# Revit family: Haworth_Tibas_Desk_MeetingTable_AP_PRELIMINARY1
name_source: partatom
category: Furniture
units: mm (PartAtom-declared; Revit-internal decimal feet)

## family parameters
Always vertical = Yes
Cut with Voids When Loaded = No
OmniClass Number = 23.40.70.14.64.11
OmniClass Title = Office Furniture
Room Calculation Point = No
Shared = No
Work Plane-Based = No

## types (2) — shared parameters
Actual Depth = 1400 mm  [stored 4.59318 ft]
Actual Height = 835 mm
Actual Width = 1400 mm  [stored 4.59318 ft]
Assembly Code = E2020200
Cable Tray Finish = Haworth _ Paint _ Metallic Silver
Cable Tray Width = 1000 mm  [stored 3.28084 ft]
Description = Haworth - Tibas - Desk - Meeting Table
Flip Top Width = 200 mm  [stored 0.656168 ft]
Leg Height = 800 mm  [stored 2.62467 ft]
Manufacturer = Haworth
Model = SYTBMNXXXX
Product URL = https://www.haworth.com
Revision Number = 1
Size = Verify Final Dim.w/ Haworth
Trim Finish = Haworth _ Polymer _ Undecided
URL = https://www.haworth.com
Warranty = http://www.haworth.com

## per-type parameters (varying)
| type | Beam Width | Cable Tray | Flip Top Cable Outlet | Flush Table | Leg Depth | Leg Width | Non Flush Table |
| 1400w x 1400d - Non Flush | 1200 mm | No | No | No | 1200 mm | 150 mm | Yes |
| 1400w x 1400d - Flush | 1400 mm  [stored 4.59318 ft] | Yes | Yes | Yes | 1400 mm  [stored 4.59318 ft] | 50 mm  [stored 0.164042 ft] | No |

note: [stored X ft] marks values corroborated as IEEE doubles in the binary element streams (Revit-internal decimal feet)

## geometry (parser evidence)
native form markers: Sweep x20
no freeform markers — native parametric forms only
